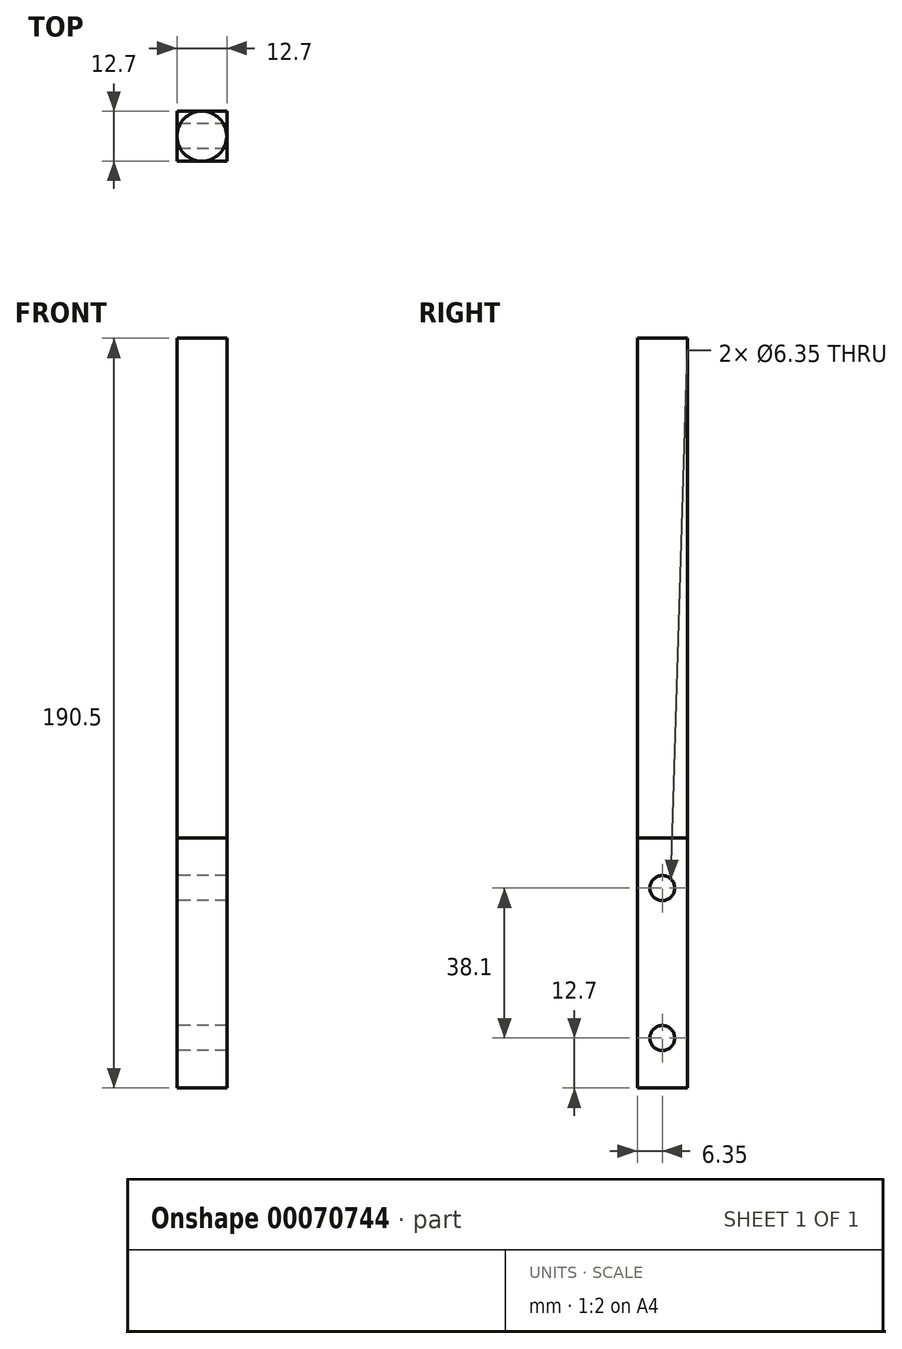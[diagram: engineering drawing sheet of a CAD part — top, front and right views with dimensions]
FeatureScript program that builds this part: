
annotation { "Feature Type Name" : "Feature", "Feature Type Description" : "" }
export const myFeature = defineFeature(function(context is Context, id is Id, definition is map)
    precondition{}
    {
        {
            var Q0;
            Q0=qCreatedBy(makeId("Top.planeOp"),FACE);
            var sketch = newSketch(context, id + "F0", { "sketchPlane" : qUnion([Q0])});
            skLineSegment(sketch, "E0.bottom", {"start": v(0, 0) * mm, "end": v(12.7, 0) * mm});
            skLineSegment(sketch, "E0.top", {"start": v(0, 12.7) * mm, "end": v(12.7, 12.7) * mm});
            skLineSegment(sketch, "E0.left", {"start": v(0, 0) * mm, "end": v(0, 12.7) * mm});
            skLineSegment(sketch, "E0.right", {"start": v(12.7, 0) * mm, "end": v(12.7, 12.7) * mm});
            skSolve(sketch);
        }
        {
            var Q0;
            Q0 = qSketchRegion(id + "F0", true);
            extrude(context, id + "F1", {"entities" : qUnion([Q0]), "depth" : 63.5 * mm});
        }
        {
            var Q0;
            Q0=makeQuery(id+"F1.opExtrude","CAP_FACE",FACE,{"disambiguationData":[OSD([sQuery(id+"F0.wireOp",EDGE,"E0.bottom"),sQuery(id+"F0.wireOp",EDGE,"E0.top"),sQuery(id+"F0.wireOp",EDGE,"E0.left"),sQuery(id+"F0.wireOp",EDGE,"E0.right")])],"isStart":false});
            var sketch = newSketch(context, id + "F2", { "sketchPlane" : qUnion([Q0])});
            skCircle(sketch, "E1", {"center": v(6.35, 6.35) * mm, "radius": 6.35 * mm});
            skPoint(sketch, "E1.centerSnap0", {"position": v(6.35, 12.7) * mm});
            skPoint(sketch, "E1.centerSnap1", {"position": v(0, 6.35) * mm});
            skSolve(sketch);
        }
        {
            var Q0;
            Q0 = qSketchRegion(id + "F2", true);
            extrude(context, id + "F3", {"entities" : qUnion([Q0]), "operationType" : NewBodyOperationType.ADD, "depth" : 127 * mm});
        }
        {
            var Q0;
            Q0=makeQuery(id+"F1.opExtrude","SWEPT_FACE",FACE,{"disambiguationData":[OSD([sQuery(id+"F0.wireOp",EDGE,"E0.left")])]});
            var sketch = newSketch(context, id + "F4", { "sketchPlane" : qUnion([Q0])});
            skCircle(sketch, "E2", {"center": v(-6.35, 12.7) * mm, "radius": 3.18 * mm});
            skPoint(sketch, "E2.centerSnap0", {"position": v(-6.35, 0) * mm});
            skCircle(sketch, "E3", {"center": v(-6.35, 50.8) * mm, "radius": 3.18 * mm});
            skSolve(sketch);
        }
        {
            var Q0;
            Q0=makeQuery(id+"F4.imprint","IMPRINT",FACE,{"disambiguationData":[TD([[makeQuery(id+"F4.imprint","IMPRINT",EDGE,{"derivedFrom":sQuery(id+"F4.wireOp",EDGE,"E2")}),1.0]])]});
            var Q1;
            Q1=makeQuery(id+"F4.imprint","IMPRINT",FACE,{"disambiguationData":[TD([[makeQuery(id+"F4.imprint","IMPRINT",EDGE,{"derivedFrom":sQuery(id+"F4.wireOp",EDGE,"E3")}),1.0]])]});
            extrude(context, id + "F5", {"entities" : qUnion([Q0, Q1]), "operationType" : NewBodyOperationType.REMOVE, "oppositeDirection" : true, "depth" : 25.4 * mm});
        }
    });
